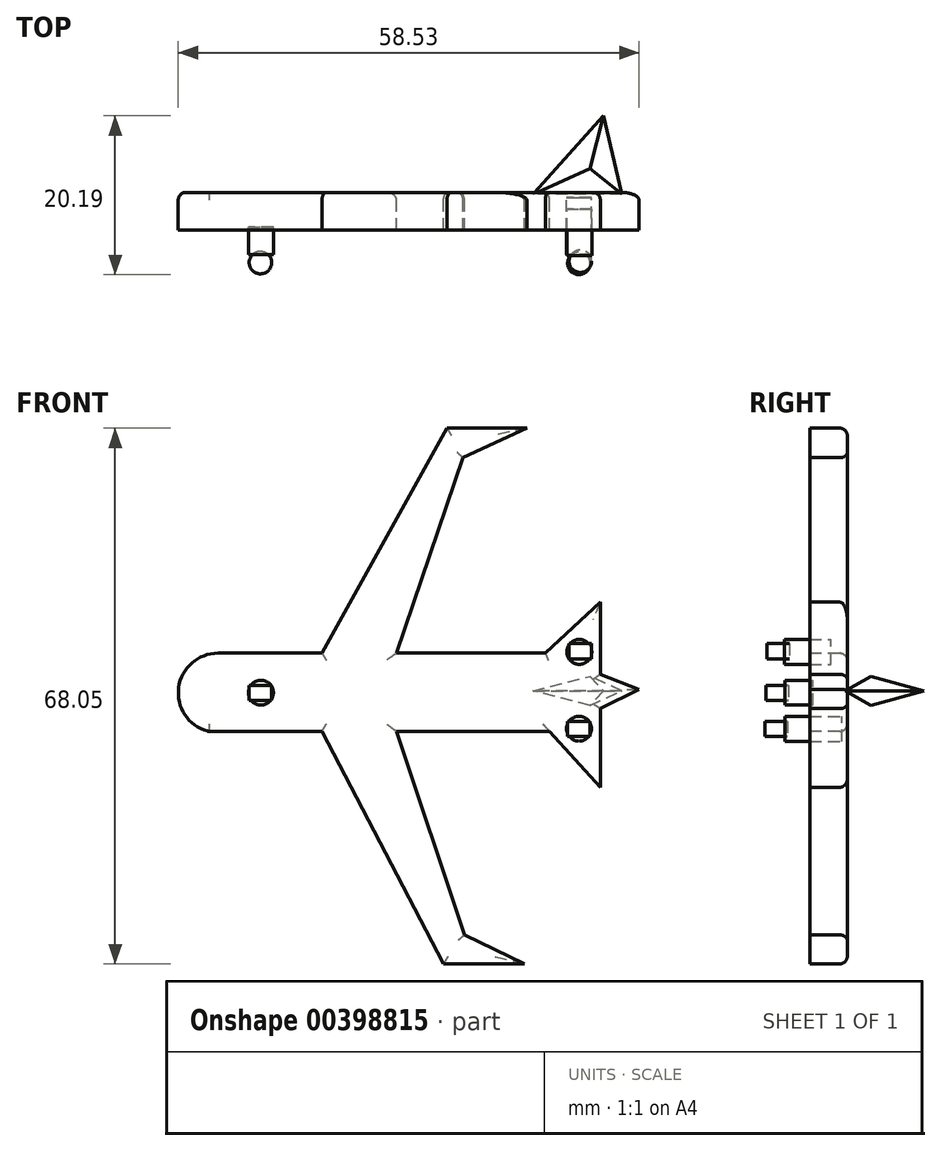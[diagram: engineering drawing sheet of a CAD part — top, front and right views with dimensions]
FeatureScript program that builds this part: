
annotation { "Feature Type Name" : "Feature", "Feature Type Description" : "" }
export const myFeature = defineFeature(function(context is Context, id is Id, definition is map)
    precondition{}
    {
        {
            var Q0;
            Q0=qCreatedBy(makeId("Front.planeOp"),FACE);
            var sketch = newSketch(context, id + "F0", { "sketchPlane" : qUnion([Q0])});
            skLineSegment(sketch, "E0", {"start": v(100.8, 31.66) * mm, "end": v(-120.95, 31.66) * mm});
            skLineSegment(sketch, "E1", {"start": v(86.68, -21.4) * mm, "end": v(-127.41, -21.4) * mm});
            skArc(sketch, "E2", {"start": v(-120.95, 31.66) * mm, "mid": v(-147.67, 8) * mm, "end": v(-127.41, -21.4) * mm});
            skLineSegment(sketch, "E3", {"start": v(-50.54, 31.66) * mm, "end": v(34.13, 184.1) * mm});
            skLineSegment(sketch, "E4", {"start": v(88.35, 184.1) * mm, "end": v(34.13, 184.1) * mm});
            skLineSegment(sketch, "E5", {"start": v(88.35, 184.1) * mm, "end": v(45, 164.05) * mm});
            skLineSegment(sketch, "E6", {"start": v(45, 164.05) * mm, "end": v(0, 31.66) * mm});
            skLineSegment(sketch, "E7", {"start": v(-50.62, -21.4) * mm, "end": v(31.9, -178.83) * mm});
            skLineSegment(sketch, "E8", {"start": v(86.57, -178.83) * mm, "end": v(31.9, -178.83) * mm});
            skLineSegment(sketch, "E9", {"start": v(86.57, -178.83) * mm, "end": v(45.95, -159.26) * mm});
            skLineSegment(sketch, "E10", {"start": v(45.95, -159.26) * mm, "end": v(0, -21.4) * mm});
            skLineSegment(sketch, "E11", {"start": v(86.68, -21.4) * mm, "end": v(103.67, -21.4) * mm});
            skLineSegment(sketch, "E12", {"start": v(103.67, -21.4) * mm, "end": v(138.06, -59.25) * mm});
            skLineSegment(sketch, "E13", {"start": v(138.06, -59.25) * mm, "end": v(138.06, -21.4) * mm});
            skLineSegment(sketch, "E14", {"start": v(100.8, 31.66) * mm, "end": v(138.06, 66.18) * mm});
            skLineSegment(sketch, "E15", {"start": v(138.06, 66.18) * mm, "end": v(138.06, 31.66) * mm});
            skLineSegment(sketch, "E16", {"start": v(138.06, -21.4) * mm, "end": v(138.06, -5.94) * mm});
            skLineSegment(sketch, "E17", {"start": v(138.06, 31.66) * mm, "end": v(138.06, 17.3) * mm});
            skLineSegment(sketch, "E18", {"start": v(138.06, 17.3) * mm, "end": v(164.25, 7.02) * mm});
            skLineSegment(sketch, "E19", {"start": v(164.25, 7.02) * mm, "end": v(138.06, -5.94) * mm});
            skSolve(sketch);
        }
        {
            var Q0;
            Q0=qCreatedBy(makeId("Top.planeOp"),FACE);
            var sketch = newSketch(context, id + "F1", { "sketchPlane" : qUnion([Q0])});
            skLineSegment(sketch, "E20", {"start": v(103.4, 13.6) * mm, "end": v(163.63, 13.6) * mm});
            skLineSegment(sketch, "E21", {"start": v(103.4, 13.6) * mm, "end": v(150.97, 66.7) * mm});
            skLineSegment(sketch, "E22", {"start": v(150.97, 66.7) * mm, "end": v(163.63, 13.6) * mm});
            skSolve(sketch);
        }
        {
            var Q0;
            Q0 = qSketchRegion(id + "F0", true);
            extrude(context, id + "F2", {"entities" : qUnion([Q0]), "depth" : 25.4 * mm});
        }
        {
            var Q0;
            Q0=makeQuery(id+"F2.opExtrude","CAP_EDGE",EDGE,{"disambiguationData":[OSD([sQuery(id+"F0.wireOp",EDGE,"E1")])],"isStart":true});
            var Q1;
            {var subQ0=sQuery(id+"F0.wireOp",EDGE,"E0");Q1=makeQuery(id+"F2.opExtrude","CAP_EDGE",EDGE,{"disambiguationData":[OSD([subQ0]),TDD([makeQuery(id+"F0.imprint","IMPRINT",EDGE,{"disambiguationData":[TD([[makeQuery(id+"F0.imprint","INTERSECT",VERTEX,{"derivedFrom":[subQ0,sQuery(id+"F0.wireOp",EDGE,"E2")]}),1.0]])],"derivedFrom":subQ0})])],"isStart":true});}
            var Q2;
            {var subQ0=sQuery(id+"F0.wireOp",EDGE,"E0");Q2=makeQuery(id+"F2.opExtrude","CAP_EDGE",EDGE,{"disambiguationData":[OSD([subQ0]),TDD([makeQuery(id+"F0.imprint","IMPRINT",EDGE,{"disambiguationData":[TD([[makeQuery(id+"F0.imprint","INTERSECT",VERTEX,{"derivedFrom":[subQ0,sQuery(id+"F0.wireOp",EDGE,"E14")]}),-1.0]])],"derivedFrom":subQ0})])],"isStart":true});}
            var Q3;
            Q3=makeQuery(id+"F2.opExtrude","CAP_EDGE",EDGE,{"disambiguationData":[OSD([sQuery(id+"F0.wireOp",EDGE,"E1"),sQuery(id+"F0.wireOp",EDGE,"E11")])],"isStart":true});
            var Q4;
            Q4=makeQuery(id+"F2.opExtrude","CAP_EDGE",EDGE,{"disambiguationData":[OSD([sQuery(id+"F0.wireOp",EDGE,"E10")])],"isStart":true});
            var Q5;
            Q5=makeQuery(id+"F2.opExtrude","CAP_EDGE",EDGE,{"disambiguationData":[OSD([sQuery(id+"F0.wireOp",EDGE,"E7")])],"isStart":true});
            var Q6;
            Q6=makeQuery(id+"F2.opExtrude","CAP_EDGE",EDGE,{"disambiguationData":[OSD([sQuery(id+"F0.wireOp",EDGE,"E3")])],"isStart":true});
            var Q7;
            Q7=makeQuery(id+"F2.opExtrude","CAP_EDGE",EDGE,{"disambiguationData":[OSD([sQuery(id+"F0.wireOp",EDGE,"E6")])],"isStart":true});
            var Q8;
            Q8=makeQuery(id+"F2.opExtrude","CAP_EDGE",EDGE,{"disambiguationData":[OSD([sQuery(id+"F0.wireOp",EDGE,"E14")])],"isStart":true});
            var Q9;
            Q9=makeQuery(id+"F2.opExtrude","CAP_EDGE",EDGE,{"disambiguationData":[OSD([sQuery(id+"F0.wireOp",EDGE,"E15"),sQuery(id+"F0.wireOp",EDGE,"E17")])],"isStart":true});
            var Q10;
            Q10=makeQuery(id+"F2.opExtrude","CAP_EDGE",EDGE,{"disambiguationData":[OSD([sQuery(id+"F0.wireOp",EDGE,"E13"),sQuery(id+"F0.wireOp",EDGE,"E16")])],"isStart":true});
            var Q11;
            Q11=makeQuery(id+"F2.opExtrude","CAP_EDGE",EDGE,{"disambiguationData":[OSD([sQuery(id+"F0.wireOp",EDGE,"E19")])],"isStart":true});
            var Q12;
            Q12=makeQuery(id+"F2.opExtrude","CAP_EDGE",EDGE,{"disambiguationData":[OSD([sQuery(id+"F0.wireOp",EDGE,"E18")])],"isStart":true});
            var Q13;
            Q13=makeQuery(id+"F2.opExtrude","CAP_EDGE",EDGE,{"disambiguationData":[OSD([sQuery(id+"F0.wireOp",EDGE,"E8")])],"isStart":true});
            var Q14;
            Q14=makeQuery(id+"F2.opExtrude","CAP_EDGE",EDGE,{"disambiguationData":[OSD([sQuery(id+"F0.wireOp",EDGE,"E9")])],"isStart":true});
            var Q15;
            Q15=makeQuery(id+"F2.opExtrude","CAP_EDGE",EDGE,{"disambiguationData":[OSD([sQuery(id+"F0.wireOp",EDGE,"E5")])],"isStart":true});
            var Q16;
            Q16=makeQuery(id+"F2.opExtrude","CAP_EDGE",EDGE,{"disambiguationData":[OSD([sQuery(id+"F0.wireOp",EDGE,"E4")])],"isStart":true});
            fillet(context, id + "F3", {"entities" : qUnion([Q0, Q1, Q2, Q3, Q4, Q5, Q6, Q7, Q8, Q9, Q10, Q11, Q12, Q13, Q14, Q15, Q16]), "radius" : 5.08 * mm, "allowEdgeOverflow" : false});
        }
        {
            var Q0;
            Q0=makeQuery(id+"F2.opExtrude","CAP_EDGE",EDGE,{"disambiguationData":[OSD([sQuery(id+"F0.wireOp",EDGE,"E2")])],"isStart":true});
            fillet(context, id + "F4", {"entities" : qUnion([Q0]), "radius" : 5.08 * mm, "tangentPropagation" : true, "allowEdgeOverflow" : false});
        }
        {
            var Q0;
            Q0=makeQuery(id+"F1.imprint","IMPRINT",FACE,{"disambiguationData":[TD([[makeQuery(id+"F1.imprint","IMPRINT",EDGE,{"derivedFrom":sQuery(id+"F1.wireOp",EDGE,"E20")}),1.0]])]});
            extrude(context, id + "F5", {"entities" : qUnion([Q0]), "endBound" : BoundingType.SYMMETRIC, "depth" : 20.32 * mm, "hasDraft" : true, "draftAngle" : 60 * degree, "draftPullDirection" : true});
        }
        {
            var Q0;
            Q0=makeQuery(id+"F5.opExtrude","SWEPT_BODY",BODY,{"disambiguationData":[OSD([sQuery(id+"F1.wireOp",EDGE,"E20"),sQuery(id+"F1.wireOp",EDGE,"E21"),sQuery(id+"F1.wireOp",EDGE,"E22")])]});
            transform(context, id + "F6", {"entities" : qUnion([Q0]), "transformType" : TransformType.TRANSLATION_3D, "dx" : -10.92 * mm, "dy" : -14.73 * mm, "dz" : 6.1 * mm, "makeCopy" : false});
        }
        {
            var Q0;
            Q0=qCreatedBy(makeId("Front.planeOp"),FACE);
            var sketch = newSketch(context, id + "F7", { "sketchPlane" : qUnion([Q0])});
            skCircle(sketch, "E23", {"center": v(-91.4, 4.86) * mm, "radius": 8.45 * mm});
            skSolve(sketch);
        }
        {
            var Q0;
            Q0=makeQuery(id+"F7.imprint","IMPRINT",FACE,{"disambiguationData":[TD([[makeQuery(id+"F7.imprint","IMPRINT",EDGE,{"derivedFrom":sQuery(id+"F7.wireOp",EDGE,"E23")}),1.0]])]});
            extrude(context, id + "F8", {"entities" : qUnion([Q0]), "depth" : 39.88 * mm, "hasSecondDirection" : true, "secondDirectionOppositeDirection" : false, "secondDirectionDepth" : 21.08 * mm});
        }
        {
            var Q0;
            Q0=makeQuery(id+"F8.opExtrude","SWEPT_BODY",BODY,{"disambiguationData":[OSD([sQuery(id+"F7.wireOp",EDGE,"E23")])]});
            transform(context, id + "F9", {"entities" : qUnion([Q0]), "transformType" : TransformType.TRANSLATION_3D, "dx" : -0.5 * mm, "dy" : -2.3 * mm, "dz" : 0 * mm, "makeCopy" : false});
        }
        {
            var Q0;
            Q0=qCreatedBy(makeId("Front.planeOp"),FACE);
            var sketch = newSketch(context, id + "F10", { "sketchPlane" : qUnion([Q0])});
            skCircle(sketch, "E24", {"center": v(-40.73, 0) * mm, "radius": 8.45 * mm});
            skSolve(sketch);
        }
        {
            var Q0;
            Q0=makeQuery(id+"F10.imprint","IMPRINT",FACE,{"disambiguationData":[TD([[makeQuery(id+"F10.imprint","IMPRINT",EDGE,{"derivedFrom":sQuery(id+"F10.wireOp",EDGE,"E24")}),1.0]])]});
            extrude(context, id + "F11", {"entities" : qUnion([Q0]), "depth" : 38.6 * mm});
        }
        {
            var Q0;
            Q0=makeQuery(id+"F11.opExtrude","SWEPT_BODY",BODY,{"disambiguationData":[OSD([sQuery(id+"F10.wireOp",EDGE,"E24")])]});
            transform(context, id + "F12", {"entities" : qUnion([Q0]), "transformType" : TransformType.TRANSLATION_3D, "dx" : 164.34 * mm, "dy" : -3.56 * mm, "dz" : -19.56 * mm, "makeCopy" : false});
        }
        {
            var Q0;
            Q0=qCreatedBy(makeId("Front.planeOp"),FACE);
            var sketch = newSketch(context, id + "F13", { "sketchPlane" : qUnion([Q0])});
            skCircle(sketch, "E25", {"center": v(178.86, 334.6) * mm, "radius": 8.45 * mm});
            skCircle(sketch, "E26", {"center": v(-46.63, -132.08) * mm, "radius": 8.45 * mm});
            skSolve(sketch);
        }
        {
            var Q0;
            Q0=makeQuery(id+"F13.imprint","IMPRINT",FACE,{"disambiguationData":[TD([[makeQuery(id+"F13.imprint","IMPRINT",EDGE,{"derivedFrom":sQuery(id+"F13.wireOp",EDGE,"E26")}),1.0]])]});
            extrude(context, id + "F14", {"entities" : qUnion([Q0]), "depth" : 31.5 * mm});
        }
        {
            var Q0;
            Q0=makeQuery(id+"F14.opExtrude","SWEPT_BODY",BODY,{"disambiguationData":[OSD([sQuery(id+"F13.wireOp",EDGE,"E26")])]});
            transform(context, id + "F15", {"entities" : qUnion([Q0]), "transformType" : TransformType.TRANSLATION_3D, "dx" : 170.43 * mm, "dy" : -11.18 * mm, "dz" : 164.6 * mm, "makeCopy" : false});
        }
        {
            var Q0;
            Q0=qCreatedBy(makeId("Top.planeOp"),FACE);
            var sketch = newSketch(context, id + "F16", { "sketchPlane" : qUnion([Q0])});
            skCircle(sketch, "E27", {"center": v(-92.73, 51.71) * mm, "radius": 7.62 * mm});
            skSolve(sketch);
        }
        {
            var Q0;
            Q0=makeQuery(id+"F16.imprint","IMPRINT",FACE,{"disambiguationData":[TD([[makeQuery(id+"F16.imprint","IMPRINT",EDGE,{"derivedFrom":sQuery(id+"F16.wireOp",EDGE,"E27")}),1.0]])]});
            extrude(context, id + "F17", {"entities" : qUnion([Q0]), "depth" : 10.4 * mm});
        }
        {
            var Q0;
            Q0=makeQuery(id+"F17.opExtrude","SWEPT_BODY",BODY,{"disambiguationData":[OSD([sQuery(id+"F16.wireOp",EDGE,"E27")])]});
            transform(context, id + "F18", {"entities" : qUnion([Q0]), "transformType" : TransformType.TRANSLATION_3D, "dx" : 0.5 * mm, "dy" : -99.31 * mm, "dz" : -0.5 * mm, "makeCopy" : false});
        }
        {
            var Q0;
            Q0=qCreatedBy(makeId("Top.planeOp"),FACE);
            var sketch = newSketch(context, id + "F19", { "sketchPlane" : qUnion([Q0])});
            skCircle(sketch, "E28", {"center": v(-71.32, 41.82) * mm, "radius": 7.62 * mm});
            skSolve(sketch);
        }
        {
            var Q0;
            Q0 = qSketchRegion(id + "F19", true);
            extrude(context, id + "F20", {"entities" : qUnion([Q0]), "depth" : 10.4 * mm});
        }
        {
            var Q0;
            Q0=makeQuery(id+"F20.opExtrude","SWEPT_BODY",BODY,{"disambiguationData":[OSD([sQuery(id+"F19.wireOp",EDGE,"E28")])]});
            transform(context, id + "F21", {"entities" : qUnion([Q0]), "transformType" : TransformType.TRANSLATION_3D, "dx" : 194.82 * mm, "dy" : -89.92 * mm, "dz" : -24.9 * mm, "makeCopy" : false});
        }
        {
            var Q0;
            Q0=qCreatedBy(makeId("Top.planeOp"),FACE);
            var sketch = newSketch(context, id + "F22", { "sketchPlane" : qUnion([Q0])});
            skCircle(sketch, "E29", {"center": v(-62.68, 55.18) * mm, "radius": 7.62 * mm});
            skSolve(sketch);
        }
        {
            var Q0;
            Q0=makeQuery(id+"F22.imprint","IMPRINT",FACE,{"disambiguationData":[TD([[makeQuery(id+"F22.imprint","IMPRINT",EDGE,{"derivedFrom":sQuery(id+"F22.wireOp",EDGE,"E29")}),1.0]])]});
            extrude(context, id + "F23", {"entities" : qUnion([Q0]), "depth" : 10.4 * mm});
        }
        {
            var Q0;
            Q0=makeQuery(id+"F23.opExtrude","SWEPT_BODY",BODY,{"disambiguationData":[OSD([sQuery(id+"F22.wireOp",EDGE,"E29")])]});
            transform(context, id + "F24", {"entities" : qUnion([Q0]), "transformType" : TransformType.TRANSLATION_3D, "dx" : 187.2 * mm, "dy" : -101.85 * mm, "dz" : 27.7 * mm, "makeCopy" : false});
        }
        {
            var Q0;
            Q0=makeQuery(id+"F2.opExtrude","SWEPT_BODY",BODY,{"disambiguationData":[OSD([sQuery(id+"F0.wireOp",EDGE,"E0"),sQuery(id+"F0.wireOp",EDGE,"E1"),sQuery(id+"F0.wireOp",EDGE,"E2"),sQuery(id+"F0.wireOp",EDGE,"E3"),sQuery(id+"F0.wireOp",EDGE,"E4"),sQuery(id+"F0.wireOp",EDGE,"E5"),sQuery(id+"F0.wireOp",EDGE,"E6"),sQuery(id+"F0.wireOp",EDGE,"E7"),sQuery(id+"F0.wireOp",EDGE,"E8"),sQuery(id+"F0.wireOp",EDGE,"E9"),sQuery(id+"F0.wireOp",EDGE,"E10"),sQuery(id+"F0.wireOp",EDGE,"E11"),sQuery(id+"F0.wireOp",EDGE,"E12"),sQuery(id+"F0.wireOp",EDGE,"E13"),sQuery(id+"F0.wireOp",EDGE,"E14"),sQuery(id+"F0.wireOp",EDGE,"E15"),sQuery(id+"F0.wireOp",EDGE,"E16"),sQuery(id+"F0.wireOp",EDGE,"E17"),sQuery(id+"F0.wireOp",EDGE,"E18"),sQuery(id+"F0.wireOp",EDGE,"E19")])]});
            var Q1;
            Q1=qCreatedBy(makeId("Origin.pointOp"),VERTEX);
            transform(context, id + "F25", {"entities" : qUnion([Q0]), "transformType" : TransformType.SCALE_UNIFORMLY, "scale" : 3 / 16, "scalePoint" : qUnion([Q1]), "makeCopy" : false});
        }
        {
            var Q0;
            Q0=makeQuery(id+"F5.*.split.splitOp","SPLIT",BODY,{"derivedFrom":makeQuery(id+"F5.opExtrude","SWEPT_BODY",BODY,{"disambiguationData":[OSD([sQuery(id+"F1.wireOp",EDGE,"E20"),sQuery(id+"F1.wireOp",EDGE,"E21"),sQuery(id+"F1.wireOp",EDGE,"E22")])]})});
            var Q1;
            Q1=qCreatedBy(makeId("Origin.pointOp"),VERTEX);
            transform(context, id + "F26", {"entities" : qUnion([Q0]), "transformType" : TransformType.SCALE_UNIFORMLY, "scale" : 3 / 16, "scalePoint" : qUnion([Q1]), "makeCopy" : false});
        }
        {
            var Q0;
            Q0=makeQuery(id+"F11.opExtrude","SWEPT_BODY",BODY,{"disambiguationData":[OSD([sQuery(id+"F10.wireOp",EDGE,"E24")])]});
            var Q1;
            Q1=qCreatedBy(makeId("Origin.pointOp"),VERTEX);
            transform(context, id + "F27", {"entities" : qUnion([Q0]), "transformType" : TransformType.SCALE_UNIFORMLY, "scale" : 3 / 16, "scalePoint" : qUnion([Q1]), "makeCopy" : false});
        }
        {
            var Q0;
            Q0=makeQuery(id+"F20.opExtrude","SWEPT_BODY",BODY,{"disambiguationData":[OSD([sQuery(id+"F19.wireOp",EDGE,"E28")])]});
            var Q1;
            Q1=qCreatedBy(makeId("Origin.pointOp"),VERTEX);
            transform(context, id + "F28", {"entities" : qUnion([Q0]), "transformType" : TransformType.SCALE_UNIFORMLY, "scale" : 3 / 16, "scalePoint" : qUnion([Q1]), "makeCopy" : false});
        }
        {
            var Q0;
            Q0=makeQuery(id+"F14.opExtrude","SWEPT_BODY",BODY,{"disambiguationData":[OSD([sQuery(id+"F13.wireOp",EDGE,"E26")])]});
            var Q1;
            Q1=qCreatedBy(makeId("Origin.pointOp"),VERTEX);
            transform(context, id + "F29", {"entities" : qUnion([Q0]), "transformType" : TransformType.SCALE_UNIFORMLY, "scale" : 3 / 16, "scalePoint" : qUnion([Q1]), "makeCopy" : false});
        }
        {
            var Q0;
            Q0=makeQuery(id+"F23.opExtrude","SWEPT_BODY",BODY,{"disambiguationData":[OSD([sQuery(id+"F22.wireOp",EDGE,"E29")])]});
            var Q1;
            Q1=qCreatedBy(makeId("Origin.pointOp"),VERTEX);
            transform(context, id + "F30", {"entities" : qUnion([Q0]), "transformType" : TransformType.SCALE_UNIFORMLY, "scale" : 3 / 16, "scalePoint" : qUnion([Q1]), "makeCopy" : false});
        }
        {
            var Q0;
            Q0=makeQuery(id+"F8.opExtrude","SWEPT_BODY",BODY,{"disambiguationData":[OSD([sQuery(id+"F7.wireOp",EDGE,"E23")])]});
            var Q1;
            Q1=qCreatedBy(makeId("Origin.pointOp"),VERTEX);
            transform(context, id + "F31", {"entities" : qUnion([Q0]), "transformType" : TransformType.SCALE_UNIFORMLY, "scale" : 3 / 16, "scalePoint" : qUnion([Q1]), "makeCopy" : false});
        }
        {
            var Q0;
            Q0=makeQuery(id+"F17.opExtrude","SWEPT_BODY",BODY,{"disambiguationData":[OSD([sQuery(id+"F16.wireOp",EDGE,"E27")])]});
            var Q1;
            Q1=qCreatedBy(makeId("Origin.pointOp"),VERTEX);
            transform(context, id + "F32", {"entities" : qUnion([Q0]), "transformType" : TransformType.SCALE_UNIFORMLY, "scale" : 3 / 16, "scalePoint" : qUnion([Q1]), "makeCopy" : false});
        }
    });
